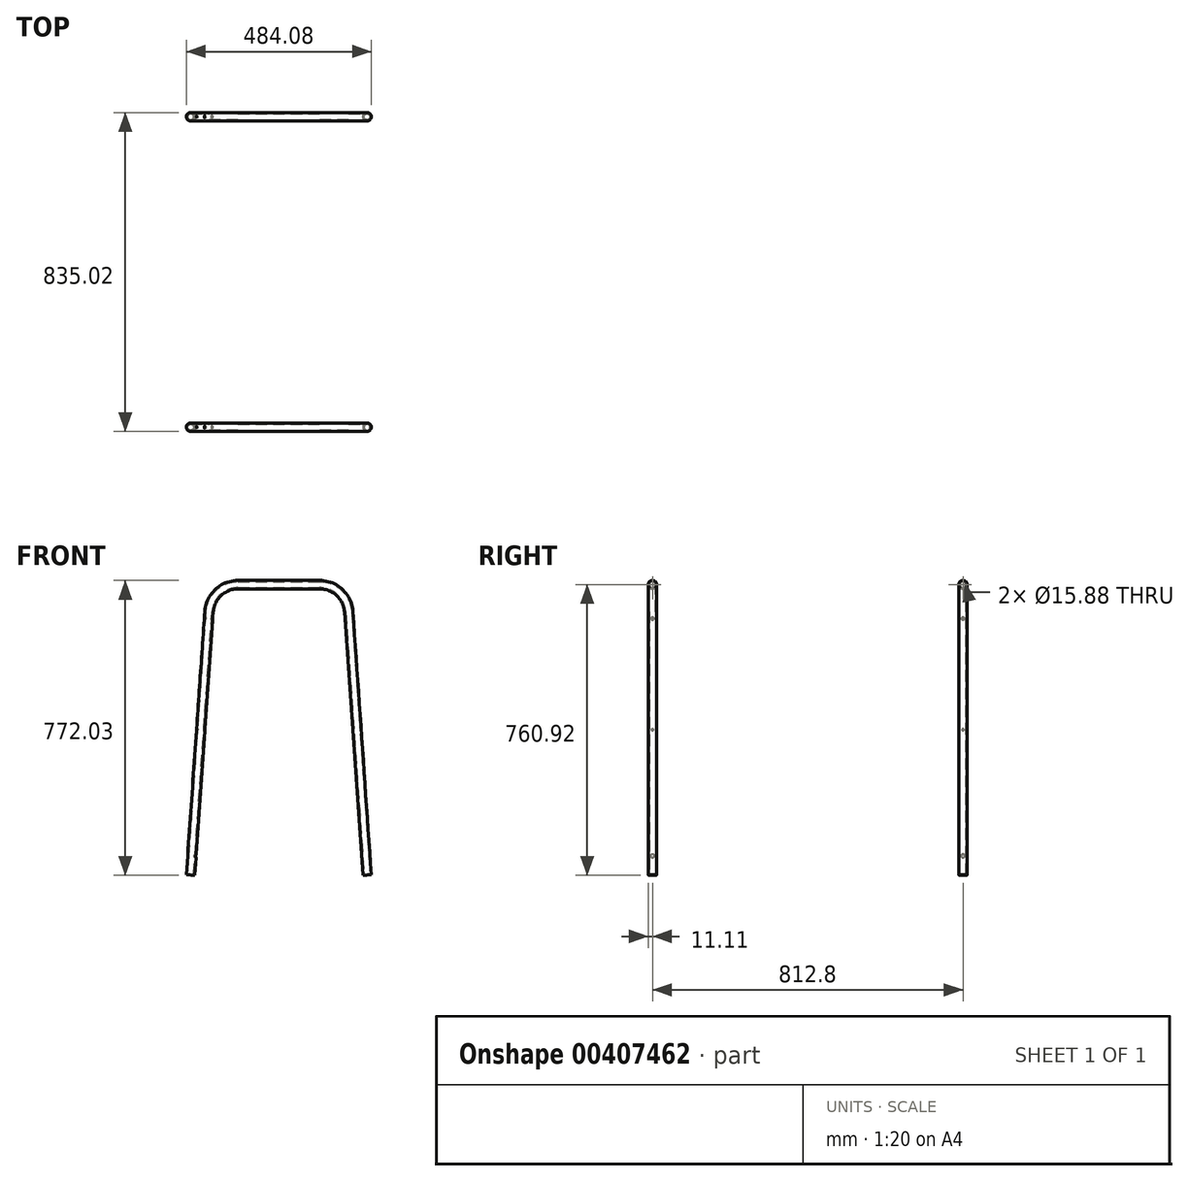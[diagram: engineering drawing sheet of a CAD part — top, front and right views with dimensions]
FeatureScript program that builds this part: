
annotation { "Feature Type Name" : "Feature", "Feature Type Description" : "" }
export const myFeature = defineFeature(function(context is Context, id is Id, definition is map)
    precondition{}
    {
        {
            var Q0;
            Q0=qCreatedBy(makeId("Front.planeOp"),FACE);
            cPlane(context, id + "F0", {"entities" : qUnion([Q0]), "cplaneType" : CPlaneType.OFFSET, "offset" : 406.4 * mm, "width" : 152.4 * mm, "height" : 152.4 * mm});
        }
        {
            var Q0;
            Q0=qCreatedBy(id+"F0.planeOp",FACE);
            var sketch = newSketch(context, id + "F1", { "sketchPlane" : qUnion([Q0])});
            skLineSegment(sketch, "E0", {"start": v(-132.14, 127) * mm, "end": v(81.34, 127) * mm});
            skLineSegment(sketch, "E1", {"start": v(-208.16, 56.12) * mm, "end": v(-256.35, -633.14) * mm});
            skLineSegment(sketch, "E2", {"start": v(157.36, 56.12) * mm, "end": v(205.55, -633.14) * mm});
            skPoint(sketch, "E3.visualSharp", {"position": v(-203.2, 127) * mm});
            skArc(sketch, "E3.filletArc", {"start": v(-132.14, 127) * mm, "mid": v(-184.11, 106.53) * mm, "end": v(-208.16, 56.12) * mm});
            skPoint(sketch, "E4.visualSharp", {"position": v(152.4, 127) * mm});
            skArc(sketch, "E4.filletArc", {"start": v(157.36, 56.12) * mm, "mid": v(133.31, 106.53) * mm, "end": v(81.34, 127) * mm});
            skLineSegment(sketch, "E5", {"start": v(0, -447.89) * mm, "end": v(0, 315.97) * mm, "construction": true});
            skLineSegment(sketch, "E6", {"start": v(-25.4, -454.34) * mm, "end": v(-25.4, 266.2) * mm});
            skSolve(sketch);
        }
        {
            var Q0;
            Q0=sQuery(id+"F1.wireOp",VERTEX,"E1.end");
            var Q1;
            Q1=sQuery(id+"F1.wireOp",EDGE,"E1");
            cPlane(context, id + "F2", {"entities" : qUnion([Q0, Q1]), "cplaneType" : CPlaneType.LINE_POINT, "offset" : 25.4 * mm, "width" : 152.4 * mm, "height" : 152.4 * mm});
        }
        {
            var Q0;
            Q0=qCreatedBy(id+"F2.planeOp",FACE);
            var sketch = newSketch(context, id + "F3", { "sketchPlane" : qUnion([Q0])});
            skCircle(sketch, "E7", {"center": v(-211.56, 406.4) * mm, "radius": 11.11 * mm});
            skCircle(sketch, "E8", {"center": v(-211.56, 406.4) * mm, "radius": 7.94 * mm});
            skSolve(sketch);
        }
        {
            var Q0;
            Q0=makeQuery(id+"F3.imprint","IMPRINT",FACE,{"disambiguationData":[TD([[makeQuery(id+"F3.imprint","IMPRINT",EDGE,{"derivedFrom":sQuery(id+"F3.wireOp",EDGE,"E7")}),1.0]])]});
            var Q1;
            Q1=sQuery(id+"F3.wireOp",EDGE,"E7");
            var Q2;
            Q2=sQuery(id+"F1.wireOp",EDGE,"E1");
            var Q3;
            Q3=sQuery(id+"F1.wireOp",EDGE,"E3.filletArc");
            var Q4;
            Q4=sQuery(id+"F1.wireOp",EDGE,"E0");
            var Q5;
            Q5=sQuery(id+"F1.wireOp",EDGE,"E4.filletArc");
            var Q6;
            Q6=sQuery(id+"F1.wireOp",EDGE,"E2");
            sweep(context, id + "F4", {"profiles" : qUnion([Q0]), "surfaceProfiles" : qUnion([Q1]), "path" : qUnion([Q2, Q3, Q4, Q5, Q6])});
        }
        {
            var Q0;
            Q0=sQuery(id+"F1.wireOp",EDGE,"E1");
            cPlane(context, id + "F5", {"entities" : qUnion([Q0]), "cplaneType" : CPlaneType.LINE_ANGLE, "offset" : 25.4 * mm, "angle" : 0 * degree, "width" : 152.4 * mm, "height" : 152.4 * mm});
        }
        {
            var Q0;
            Q0=qCreatedBy(id+"F5.planeOp",FACE);
            var sketch = newSketch(context, id + "F6", { "sketchPlane" : qUnion([Q0])});
            skCircle(sketch, "E9", {"center": v(406.4, -598.68) * mm, "radius": 4.76 * mm});
            skSolve(sketch);
        }
        {
            var Q0;
            Q0 = qSketchRegion(id + "F6", true);
            extrude(context, id + "F7", {"entities" : qUnion([Q0]), "operationType" : NewBodyOperationType.REMOVE, "oppositeDirection" : true, "depth" : 25.4 * mm});
        }
        {
            var Q0;
            Q0=qCreatedBy(id+"F5.planeOp",FACE);
            var sketch = newSketch(context, id + "F8", { "sketchPlane" : qUnion([Q0])});
            skCircle(sketch, "E10", {"center": v(406.4, 23.68) * mm, "radius": 3.18 * mm});
            skCircle(sketch, "E11", {"center": v(406.4, -268.42) * mm, "radius": 1.98 * mm});
            skSolve(sketch);
        }
        {
            var Q0;
            Q0 = qSketchRegion(id + "F8", true);
            extrude(context, id + "F9", {"entities" : qUnion([Q0]), "operationType" : NewBodyOperationType.REMOVE, "oppositeDirection" : true, "depth" : 25.4 * mm, "hasSecondDirection" : true, "secondDirectionOppositeDirection" : false, "secondDirectionDepth" : 25.4 * mm});
        }
        {
            var Q0;
            Q0=sQuery(id+"F1.wireOp",EDGE,"E6");
            cPlane(context, id + "F10", {"entities" : qUnion([Q0]), "cplaneType" : CPlaneType.LINE_ANGLE, "offset" : 25.4 * mm, "angle" : 0 * degree, "width" : 152.4 * mm, "height" : 152.4 * mm});
        }
        {
            var Q0;
            Q0=qCreatedBy(id+"F0.planeOp",FACE);
            var sketch = newSketch(context, id + "F11", { "sketchPlane" : qUnion([Q0])});
            skLineSegment(sketch, "E12", {"start": v(-199.02, 27.5) * mm, "end": v(-29.37, 0.63) * mm, "construction": true});
            skLineSegment(sketch, "E13", {"start": v(-25.4, 0) * mm, "end": v(-242.32, 0) * mm, "construction": true});
            skLineSegment(sketch, "E14", {"start": v(-197.07, 55.34) * mm, "end": v(-245.27, -633.92) * mm});
            skLineSegment(sketch, "E15", {"start": v(-197.07, 55.34) * mm, "end": v(-245.27, -633.92) * mm, "construction": true});
            skLineSegment(sketch, "E16", {"start": v(-25.4, 0) * mm, "end": v(-25.4, -28.07) * mm, "construction": true});
            skLineSegment(sketch, "E17.MirrorCS", {"start": v(148.22, 27.5) * mm, "end": v(-21.43, 0.63) * mm, "construction": true});
            skPoint(sketch, "E18.visualSharp", {"position": v(-25.4, 0) * mm});
            skArc(sketch, "E18.filletArc", {"start": v(-29.37, 0.63) * mm, "mid": v(-25.4, 0.32) * mm, "end": v(-21.43, 0.63) * mm, "construction": true});
            skSolve(sketch);
        }
        {
            var Q0;
            Q0=makeQuery(id+"F4.opSweep","SWEPT_BODY",BODY,{"disambiguationData":[OSD([sQuery(id+"F1.wireOp",EDGE,"E2"),sQuery(id+"F3.wireOp",EDGE,"E7")])]});
            var Q1;
            Q1=qCreatedBy(makeId("Front.planeOp"),FACE);
            mirror(context, id + "F12", {"entities" : qUnion([Q0]), "mirrorPlane" : qUnion([Q1])});
        }
    });
